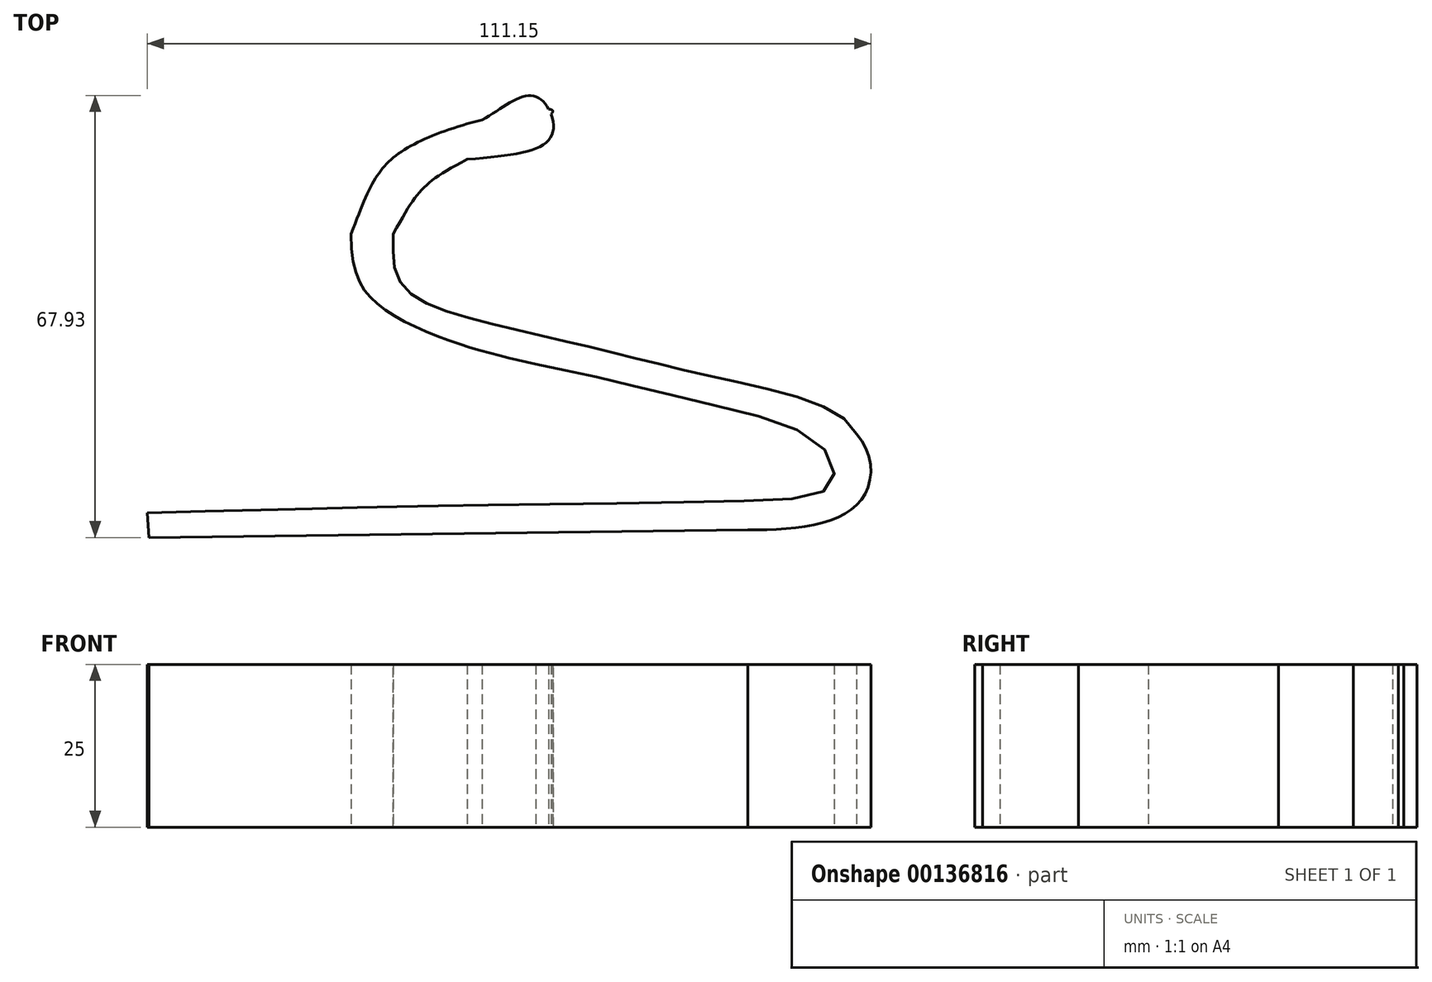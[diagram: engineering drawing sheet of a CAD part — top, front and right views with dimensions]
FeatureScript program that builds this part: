
annotation { "Feature Type Name" : "Feature", "Feature Type Description" : "" }
export const myFeature = defineFeature(function(context is Context, id is Id, definition is map)
    precondition{}
    {
        {
            var Q0;
            Q0=qCreatedBy(makeId("Top.planeOp"),FACE);
            var sketch = newSketch(context, id + "F0", { "sketchPlane" : qUnion([Q0])});
            skFitSpline(sketch, "E0", {"points": [v(-28.36, 0) * mm, v(-23.57, -11.32) * mm, v(-10.13, -17.4) * mm, v(0, -19.98) * mm], "startDerivative": vector(0, -55.84) * mm, "endDerivative": vector(32.27, -7.52) * mm});
            skFitSpline(sketch, "E1", {"points": [v(0, -19.98) * mm, v(10.31, -22.19) * mm, v(27.8, -26.42) * mm, v(43.83, -32.5) * mm, v(45.48, -38.4) * mm, v(32.4, -40.97) * mm, v(-10.13, -41.7) * mm, v(-29.28, -42.08) * mm, v(-59.66, -42.81) * mm], "startDerivative": vector(102.14, -20.83) * mm, "endDerivative": vector(-205.79, -5.4) * mm});
            skFitSpline(sketch, "E2", {"points": [v(-21.87, 0) * mm, v(-20.48, -7.9) * mm, v(-8.78, -13.25) * mm, v(10, -17.76) * mm, v(29.24, -22.36) * mm, v(49.27, -30.72) * mm], "startDerivative": vector(-2.13, -60.67) * mm, "endDerivative": vector(25.19, -59.9) * mm});
            skFitSpline(sketch, "E3", {"points": [v(49.27, -30.72) * mm, v(50.93, -39.23) * mm, v(45.06, -44.08) * mm, v(32.61, -45.46) * mm], "startDerivative": vector(22.53, -24.23) * mm, "endDerivative": vector(-32.73, 0) * mm});
            skLineSegment(sketch, "E4", {"start": v(32.61, -45.46) * mm, "end": v(-59.44, -46.64) * mm});
            skLineSegment(sketch, "E5", {"start": v(-59.66, -42.81) * mm, "end": v(-59.44, -46.64) * mm});
            skPoint(sketch, "E6.3.internal.snap0", {"position": v(-8.25, 17.54) * mm});
            skFitSpline(sketch, "E7", {"points": [v(-21.87, 0) * mm, v(-17.3, 7.01) * mm, v(-10.5, 11.5) * mm, v(2.63, 18.86) * mm, v(-8.25, 17.54) * mm, v(-21.87, 11.75) * mm, v(-28.36, 0) * mm], "startDerivative": vector(44.2, 81.24) * mm, "endDerivative": vector(-41.66, -109.4) * mm});
            skLineSegment(sketch, "E8.trimOffspring", {"start": v(2.52, 19.06) * mm, "end": v(2.52, 19.06) * mm});
            skFitSpline(sketch, "E9", {"points": [v(-21.87, 11.75) * mm, v(-8.25, 17.54) * mm, v(0, 21.15) * mm, v(2.63, 15.65) * mm, v(-10.5, 11.5) * mm], "startDerivative": vector(51.38, 25.4) * mm, "endDerivative": vector(-79.68, -6.33) * mm});
            skSolve(sketch);
        }
        {
            var Q0;
            Q0 = qSketchRegion(id + "F0", true);
            extrude(context, id + "F1", {"entities" : qUnion([Q0]), "depth" : 25 * mm});
        }
    });
